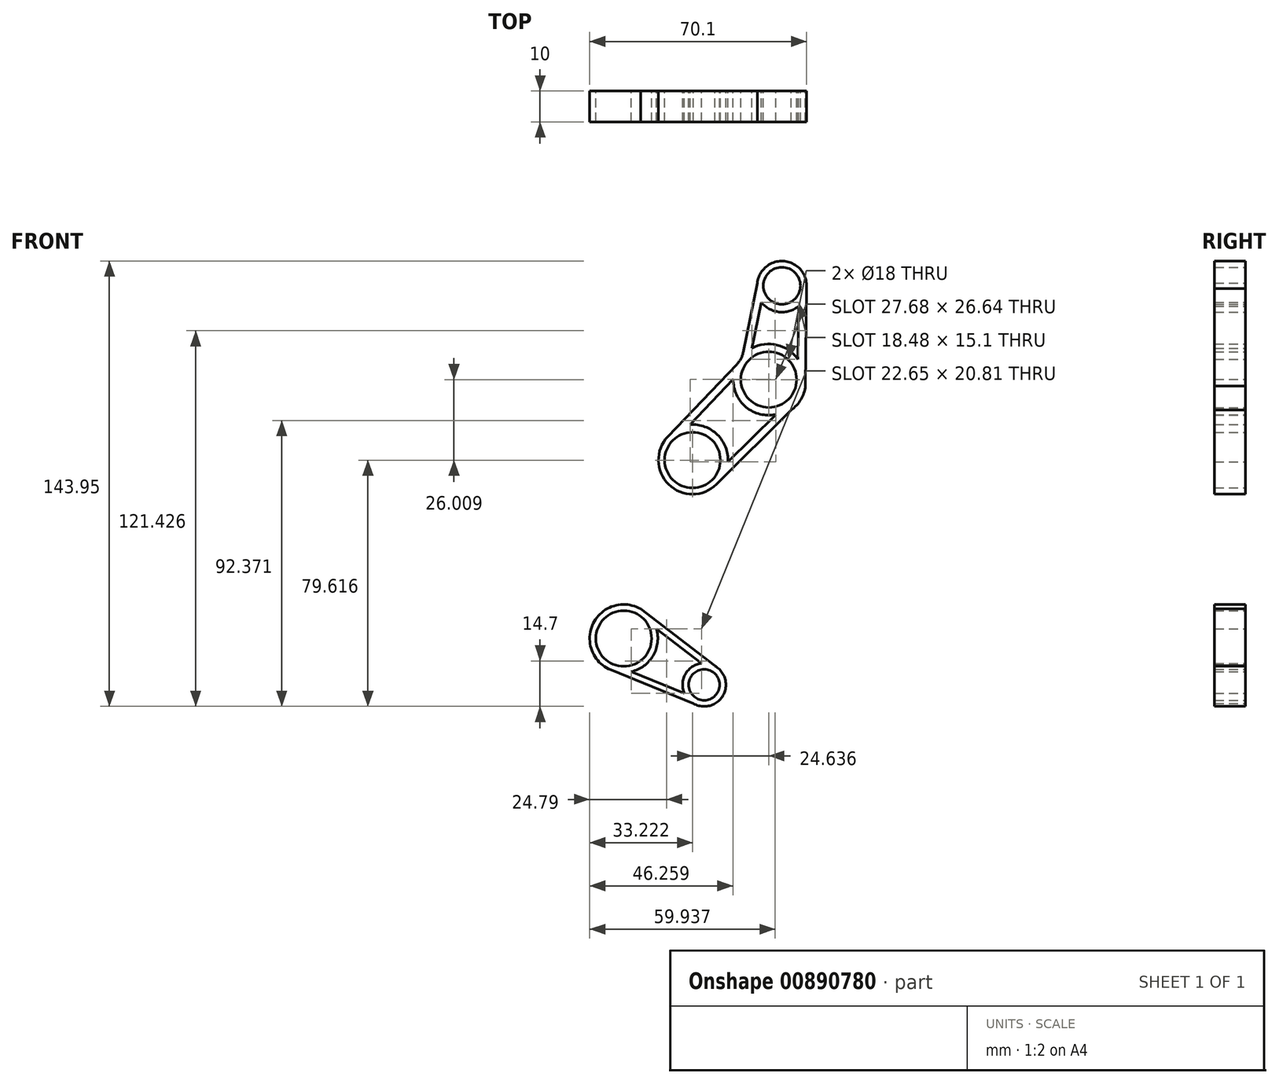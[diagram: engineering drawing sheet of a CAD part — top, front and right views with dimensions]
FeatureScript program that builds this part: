
annotation { "Feature Type Name" : "Feature", "Feature Type Description" : "" }
export const myFeature = defineFeature(function(context is Context, id is Id, definition is map)
    precondition{}
    {
        {
            var Q0;
            Q0=qCreatedBy(makeId("Front.planeOp"),FACE);
            var sketch = newSketch(context, id + "F0", { "sketchPlane" : qUnion([Q0])});
            skLineSegment(sketch, "E0", {"start": v(0, 0) * mm, "end": v(395.95, 0) * mm});
            skLineSegment(sketch, "E1.MirrorCS", {"start": v(388.54, -1.2) * mm, "end": v(13.14, -61.88) * mm});
            skCircle(sketch, "E2", {"center": v(395.95, 0) * mm, "radius": 7.5 * mm});
            skLineSegment(sketch, "E3.MirrorCS", {"start": v(390.24, -4.86) * mm, "end": v(9.54, -59.47) * mm});
            skCircle(sketch, "E4", {"center": v(-38.34, -40.57) * mm, "radius": 9 * mm});
            skCircle(sketch, "E5", {"center": v(-16.12, 17.09) * mm, "radius": 9 * mm});
            skCircle(sketch, "E6", {"center": v(12.76, 73.42) * mm, "radius": 6 * mm});
            skCircle(sketch, "E7", {"center": v(-12.34, -55.53) * mm, "radius": 5 * mm});
            skLineSegment(sketch, "E8.trimOffspring", {"start": v(11.9, -61.15) * mm, "end": v(392.34, -6.58) * mm});
            skLineSegment(sketch, "E9", {"start": v(19.12, -65.9) * mm, "end": v(9.54, -59.47) * mm});
            skPoint(sketch, "E10.orphan", {"position": v(0, -78.43) * mm});
            skPoint(sketch, "E11.trimOffspring.end.orphan", {"position": v(-61.82, -60.65) * mm});
            skArc(sketch, "E12", {"start": v(-32.85, -31.04) * mm, "mid": v(-48.2, -35.7) * mm, "end": v(-42.57, -50.72) * mm});
            skLineSegment(sketch, "E13", {"start": v(3.45, -73.18) * mm, "end": v(3.84, -73.38) * mm});
            skArc(sketch, "E14", {"start": v(-24.08, 24.68) * mm, "mid": v(-23.82, 9.23) * mm, "end": v(-8.36, 9.28) * mm});
            skArc(sketch, "E15", {"start": v(20.71, 72.57) * mm, "mid": v(13.6, 81.37) * mm, "end": v(4.8, 74.27) * mm});
            skLineSegment(sketch, "E16", {"start": v(0.23, 51.92) * mm, "end": v(4.8, 74.27) * mm});
            skLineSegment(sketch, "E17", {"start": v(-1.82, 48) * mm, "end": v(-24.08, 24.68) * mm});
            skLineSegment(sketch, "E18", {"start": v(20.71, 72.57) * mm, "end": v(20.37, 41.09) * mm});
            skLineSegment(sketch, "E19", {"start": v(15.73, 33.24) * mm, "end": v(-8.36, 9.28) * mm});
            skArc(sketch, "E20.filletArc", {"start": v(-1.82, 48) * mm, "mid": v(-0.52, 49.82) * mm, "end": v(0.23, 51.92) * mm});
            skArc(sketch, "E21.trimOffspring", {"start": v(15.73, 33.24) * mm, "mid": v(19.4, 37.59) * mm, "end": v(20.4, 43.18) * mm});
            skCircle(sketch, "E22", {"center": v(8.52, 43.1) * mm, "radius": 9 * mm});
            skLineSegment(sketch, "E23", {"start": v(-8.85, -49.47) * mm, "end": v(-8.83, -49.44) * mm});
            skLineSegment(sketch, "E24", {"start": v(-8.83, -49.44) * mm, "end": v(-8.85, -49.47) * mm});
            skArc(sketch, "E25", {"start": v(-15.83, -61.6) * mm, "mid": v(-6.27, -59.03) * mm, "end": v(-8.85, -49.47) * mm});
            skLineSegment(sketch, "E26", {"start": v(-32.85, -31.04) * mm, "end": v(-8.83, -49.44) * mm});
            skLineSegment(sketch, "E27", {"start": v(-15.83, -61.6) * mm, "end": v(-42.57, -50.72) * mm});
            skSolve(sketch);
        }
        {
            var Q0;
            Q0=makeQuery(id+"F0.imprint","IMPRINT",FACE,{"disambiguationData":[TD([[makeQuery(id+"F0.imprint","IMPRINT",EDGE,{"derivedFrom":sQuery(id+"F0.wireOp",EDGE,"E4")}),-1.0]])]});
            extrude(context, id + "F1", {"entities" : qUnion([Q0]), "depth" : 10 * mm, "offsetDistance" : 25 * mm});
        }
        {
            var Q0;
            Q0=makeQuery(id+"F1.opExtrude","CAP_FACE",FACE,{"disambiguationData":[OSD([sQuery(id+"F0.wireOp",EDGE,"E4"),sQuery(id+"F0.wireOp",EDGE,"E7"),sQuery(id+"F0.wireOp",EDGE,"E9"),sQuery(id+"F0.wireOp",EDGE,"ea858ae1-9d48-477a-8e67-d634a49d5d8b2"),sQuery(id+"F0.wireOp",EDGE,"E12"),sQuery(id+"F0.wireOp",EDGE,"f425bace-6fc5-4c1a-a629-fccbde3e67020.MirrorCS"),sQuery(id+"F0.wireOp",EDGE,"E13")])],"isStart":false});
            var Q1;
            Q1=makeQuery(id+"F1.opExtrude","CAP_FACE",FACE,{"disambiguationData":[OSD([sQuery(id+"F0.wireOp",EDGE,"E4"),sQuery(id+"F0.wireOp",EDGE,"E7"),sQuery(id+"F0.wireOp",EDGE,"E9"),sQuery(id+"F0.wireOp",EDGE,"ea858ae1-9d48-477a-8e67-d634a49d5d8b2"),sQuery(id+"F0.wireOp",EDGE,"E12"),sQuery(id+"F0.wireOp",EDGE,"f425bace-6fc5-4c1a-a629-fccbde3e67020.MirrorCS"),sQuery(id+"F0.wireOp",EDGE,"E13")])],"isStart":true});
            shell(context, id + "F2", {"entities" : qUnion([Q0, Q1]), "thickness" : 2 * mm});
        }
        {
            var Q0;
            Q0=makeQuery(id+"F0.imprint","IMPRINT",FACE,{"disambiguationData":[TD([[makeQuery(id+"F0.imprint","IMPRINT",EDGE,{"derivedFrom":sQuery(id+"F0.wireOp",EDGE,"E5")}),-1.0]])]});
            extrude(context, id + "F3", {"entities" : qUnion([Q0]), "depth" : 10 * mm, "offsetDistance" : 25 * mm});
        }
        {
            var Q0;
            Q0=makeQuery(id+"F3.opExtrude","CAP_FACE",FACE,{"disambiguationData":[OSD([sQuery(id+"F0.wireOp",EDGE,"CrvWynaZ-aqLM-KX7b-LUcS-FfVIpOYZxYcc"),sQuery(id+"F0.wireOp",EDGE,"E5"),sQuery(id+"F0.wireOp",EDGE,"GjR43RZ9-UDE2-HZiX-8KiQ-sVBls7jFRs4G"),sQuery(id+"F0.wireOp",EDGE,"E6"),sQuery(id+"F0.wireOp",EDGE,"mlVH374N-pKus-W8wV-pyRV-szXBPHkUVvSG"),sQuery(id+"F0.wireOp",EDGE,"8CifOn3n-RK0J-n18j-87bU-8gnxe0dmkPtp"),sQuery(id+"F0.wireOp",EDGE,"DjpIGxOq-CZRw-i48M-6fSc-WAb9UVmQlPoP"),sQuery(id+"F0.wireOp",EDGE,"6eIkVaxt-kI0E-dSOl-LkaL-88jh7X9T7JLC"),sQuery(id+"F0.wireOp",EDGE,"lH7HEcQs-HaEC-jnBp-f0KN-cJviILrywWs5"),sQuery(id+"F0.wireOp",EDGE,"YtismJ5y-lsWL-ai9l-5Vfq-dqY4oej1wszR"),sQuery(id+"F0.wireOp",EDGE,"8dae10db-eadf-4b6d-b4c8-5a003e8343bc.filletArc")])],"isStart":false});
            var Q1;
            Q1=makeQuery(id+"F3.opExtrude","CAP_FACE",FACE,{"disambiguationData":[OSD([sQuery(id+"F0.wireOp",EDGE,"CrvWynaZ-aqLM-KX7b-LUcS-FfVIpOYZxYcc"),sQuery(id+"F0.wireOp",EDGE,"E5"),sQuery(id+"F0.wireOp",EDGE,"GjR43RZ9-UDE2-HZiX-8KiQ-sVBls7jFRs4G"),sQuery(id+"F0.wireOp",EDGE,"E6"),sQuery(id+"F0.wireOp",EDGE,"mlVH374N-pKus-W8wV-pyRV-szXBPHkUVvSG"),sQuery(id+"F0.wireOp",EDGE,"8CifOn3n-RK0J-n18j-87bU-8gnxe0dmkPtp"),sQuery(id+"F0.wireOp",EDGE,"DjpIGxOq-CZRw-i48M-6fSc-WAb9UVmQlPoP"),sQuery(id+"F0.wireOp",EDGE,"6eIkVaxt-kI0E-dSOl-LkaL-88jh7X9T7JLC"),sQuery(id+"F0.wireOp",EDGE,"lH7HEcQs-HaEC-jnBp-f0KN-cJviILrywWs5"),sQuery(id+"F0.wireOp",EDGE,"YtismJ5y-lsWL-ai9l-5Vfq-dqY4oej1wszR"),sQuery(id+"F0.wireOp",EDGE,"8dae10db-eadf-4b6d-b4c8-5a003e8343bc.filletArc")])],"isStart":true});
            shell(context, id + "F4", {"entities" : qUnion([Q0, Q1]), "thickness" : 2.5 * mm});
        }
    });
